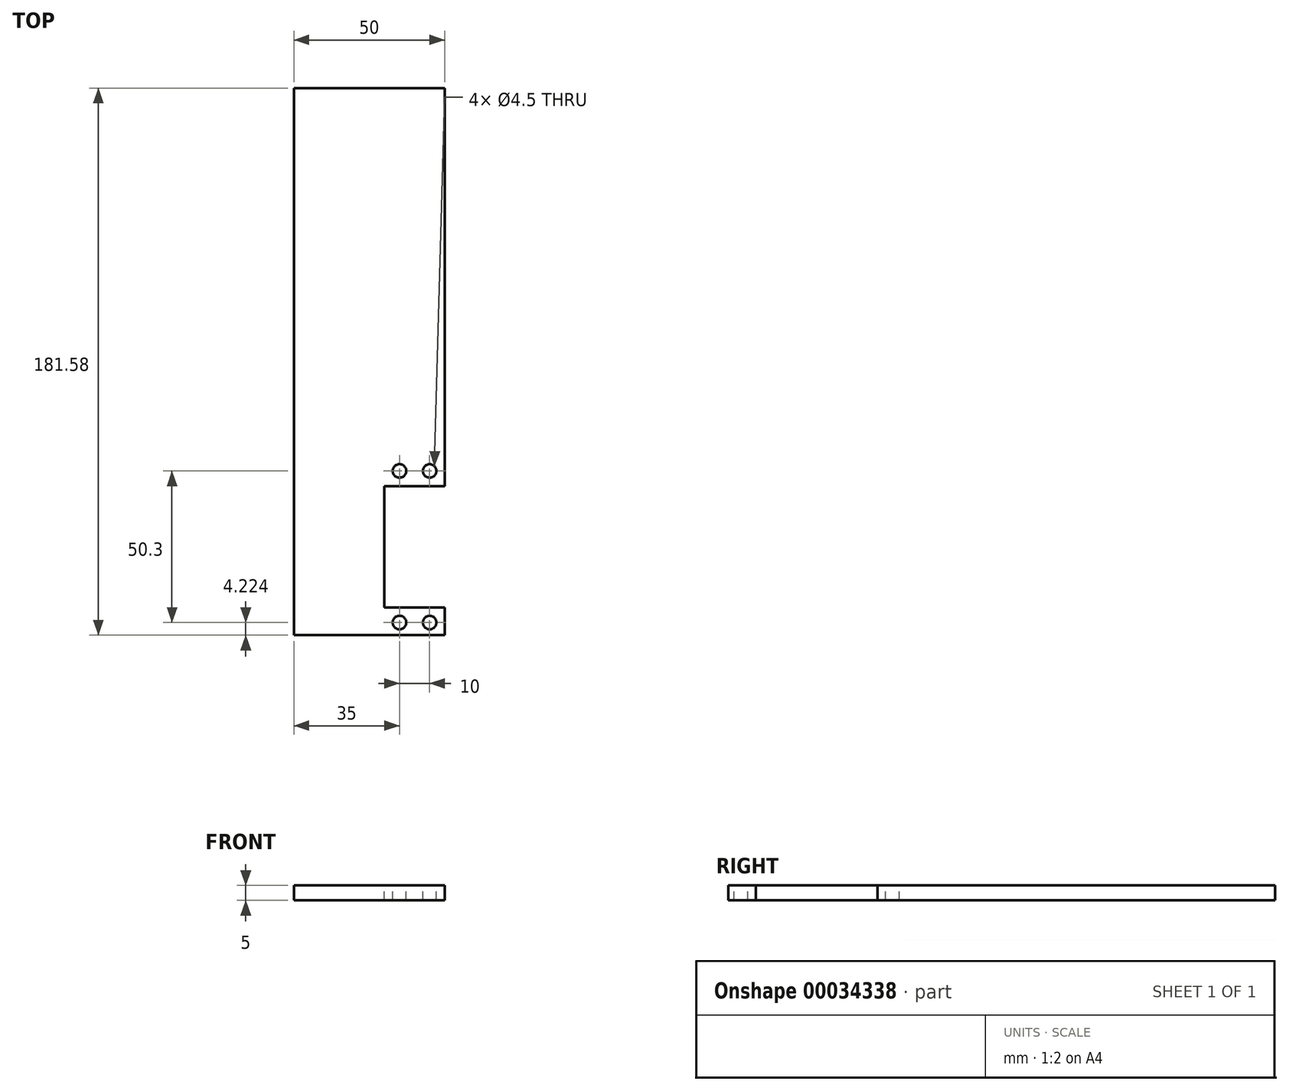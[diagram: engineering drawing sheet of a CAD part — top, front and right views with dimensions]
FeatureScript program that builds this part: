
annotation { "Feature Type Name" : "Feature", "Feature Type Description" : "" }
export const myFeature = defineFeature(function(context is Context, id is Id, definition is map)
    precondition{}
    {
        {
            var Q0;
            Q0=qCreatedBy(makeId("Top.planeOp"),FACE);
            var sketch = newSketch(context, id + "F0", { "sketchPlane" : qUnion([Q0])});
            skLineSegment(sketch, "E0.rect.bottom", {"start": v(25, 90.8) * mm, "end": v(-25, 90.8) * mm});
            skLineSegment(sketch, "E0.rect.top", {"start": v(25, -90.8) * mm, "end": v(-25, -90.8) * mm});
            skLineSegment(sketch, "E0.rect.left", {"start": v(25, 90.8) * mm, "end": v(25, -90.8) * mm});
            skLineSegment(sketch, "E0.rect.right", {"start": v(-25, 90.8) * mm, "end": v(-25, -90.8) * mm});
            skPoint(sketch, "E0.rect.middle", {"position": v(0, 0) * mm});
            skSolve(sketch);
        }
        {
            var Q0;
            Q0=makeQuery(id+"F0.imprint","IMPRINT",FACE,{"disambiguationData":[TD([[makeQuery(id+"F0.imprint","IMPRINT",EDGE,{"derivedFrom":sQuery(id+"F0.wireOp",EDGE,"E0.rect.bottom")}),1.0]])]});
            extrude(context, id + "F1", {"entities" : qUnion([Q0]), "depth" : 5 * mm});
        }
        {
            var Q0;
            Q0=makeQuery(id+"F1.opExtrude","CAP_FACE",FACE,{"disambiguationData":[OSD([sQuery(id+"F0.wireOp",EDGE,"E0.rect.bottom"),sQuery(id+"F0.wireOp",EDGE,"E0.rect.top"),sQuery(id+"F0.wireOp",EDGE,"E0.rect.left"),sQuery(id+"F0.wireOp",EDGE,"E0.rect.right")])],"isStart":false});
            var sketch = newSketch(context, id + "F2", { "sketchPlane" : qUnion([Q0])});
            skLineSegment(sketch, "E1.bottom", {"start": v(25, -81.57) * mm, "end": v(5, -81.57) * mm});
            skLineSegment(sketch, "E1.top", {"start": v(25, -41.27) * mm, "end": v(5, -41.27) * mm});
            skLineSegment(sketch, "E1.left", {"start": v(25, -81.57) * mm, "end": v(25, -41.27) * mm});
            skLineSegment(sketch, "E1.right", {"start": v(5, -81.57) * mm, "end": v(5, -41.27) * mm});
            skCircle(sketch, "E2", {"center": v(10, -36.27) * mm, "radius": 2.25 * mm});
            skCircle(sketch, "E3", {"center": v(20, -36.27) * mm, "radius": 2.25 * mm});
            skCircle(sketch, "E4", {"center": v(10, -86.57) * mm, "radius": 2.25 * mm});
            skCircle(sketch, "E5", {"center": v(20, -86.57) * mm, "radius": 2.25 * mm});
            skSolve(sketch);
        }
        {
            var Q0;
            Q0=makeQuery(id+"F2.imprint","IMPRINT",FACE,{"disambiguationData":[TD([[makeQuery(id+"F2.imprint","IMPRINT",EDGE,{"derivedFrom":sQuery(id+"F2.wireOp",EDGE,"E1.bottom")}),-1.0]])]});
            var Q1;
            Q1=makeQuery(id+"F2.imprint","IMPRINT",FACE,{"disambiguationData":[TD([[makeQuery(id+"F2.imprint","IMPRINT",EDGE,{"derivedFrom":sQuery(id+"F2.wireOp",EDGE,"E2")}),1.0]])]});
            var Q2;
            Q2=makeQuery(id+"F2.imprint","IMPRINT",FACE,{"disambiguationData":[TD([[makeQuery(id+"F2.imprint","IMPRINT",EDGE,{"derivedFrom":sQuery(id+"F2.wireOp",EDGE,"E3")}),1.0]])]});
            var Q3;
            Q3=makeQuery(id+"F2.imprint","IMPRINT",FACE,{"disambiguationData":[TD([[makeQuery(id+"F2.imprint","IMPRINT",EDGE,{"derivedFrom":sQuery(id+"F2.wireOp",EDGE,"E5")}),1.0]])]});
            var Q4;
            Q4=makeQuery(id+"F2.imprint","IMPRINT",FACE,{"disambiguationData":[TD([[makeQuery(id+"F2.imprint","IMPRINT",EDGE,{"derivedFrom":sQuery(id+"F2.wireOp",EDGE,"E4")}),1.0]])]});
            extrude(context, id + "F3", {"entities" : qUnion([Q0, Q1, Q2, Q3, Q4]), "operationType" : NewBodyOperationType.REMOVE, "oppositeDirection" : true, "depth" : 25 * mm});
        }
    });
